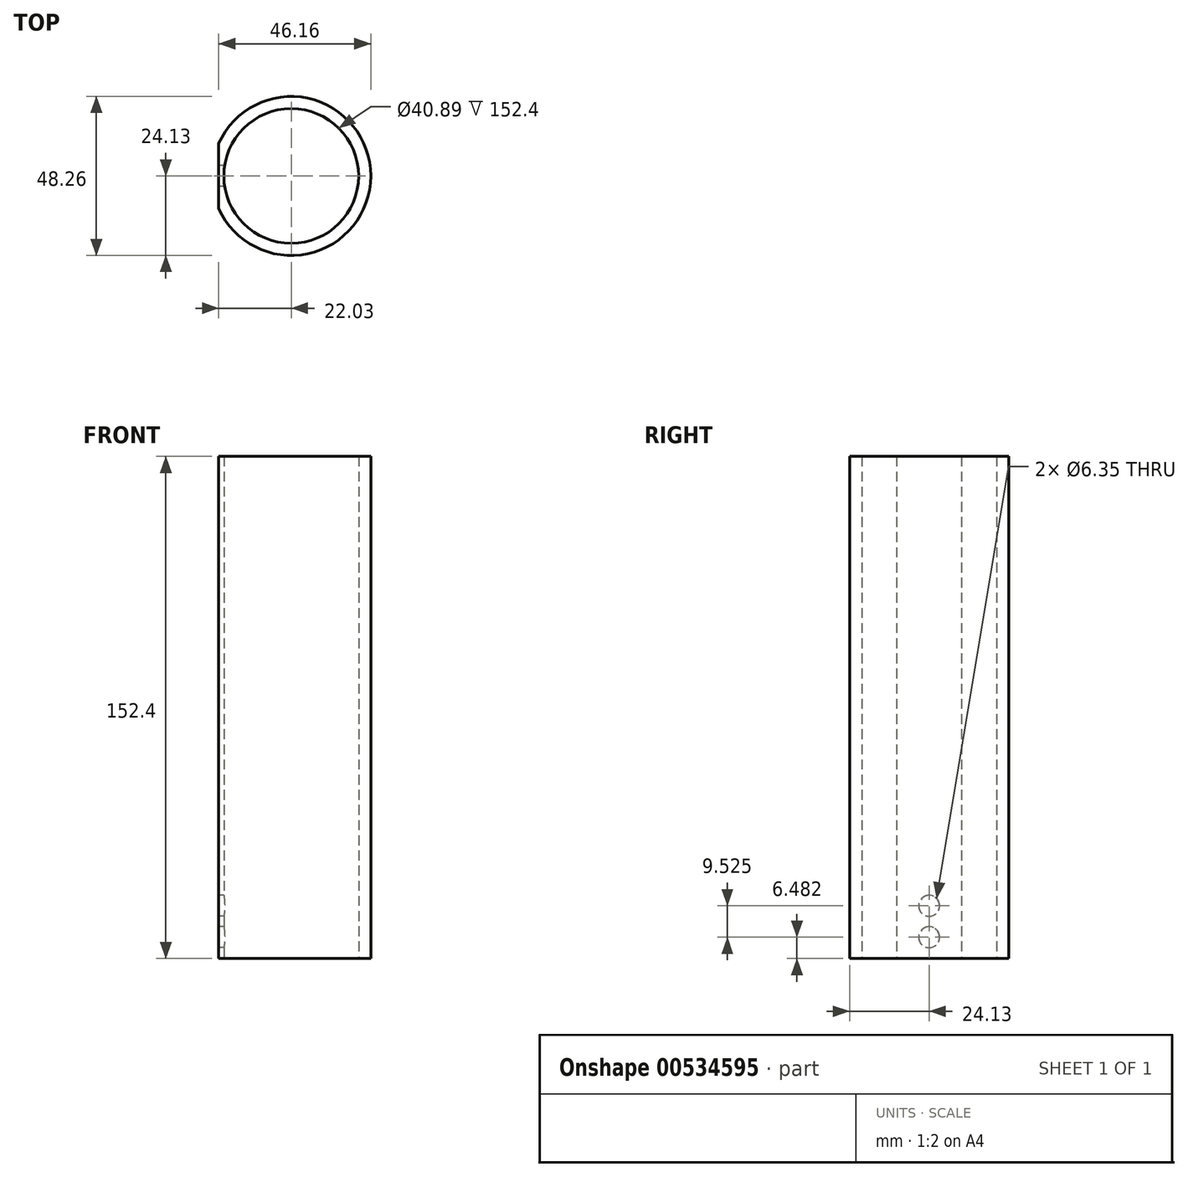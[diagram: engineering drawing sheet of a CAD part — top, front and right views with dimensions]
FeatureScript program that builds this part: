
annotation { "Feature Type Name" : "Feature", "Feature Type Description" : "" }
export const myFeature = defineFeature(function(context is Context, id is Id, definition is map)
    precondition{}
    {
        {
            var Q0;
            Q0=qCreatedBy(makeId("Top.planeOp"),FACE);
            var sketch = newSketch(context, id + "F0", { "sketchPlane" : qUnion([Q0])});
            skCircle(sketch, "E0", {"center": v(0, 0) * mm, "radius": 20.45 * mm});
            skCircle(sketch, "E1", {"center": v(0, 0) * mm, "radius": 24.13 * mm});
            skLineSegment(sketch, "E2.left", {"start": v(-22.03, 9.85) * mm, "end": v(-22.03, -9.85) * mm});
            skSolve(sketch);
        }
        {
            var Q0;
            Q0=makeQuery(id+"F0.imprint","IMPRINT",FACE,{"disambiguationData":[TD([[makeQuery(id+"F0.imprint","IMPRINT",EDGE,{"derivedFrom":sQuery(id+"F0.wireOp",EDGE,"E0")}),-1.0]])]});
            extrude(context, id + "F1", {"entities" : qUnion([Q0]), "depth" : 152.4 * mm, "offsetDistance" : 25.4 * mm});
        }
        {
            var Q0;
            Q0=makeQuery(id+"F1.opExtrude","SWEPT_FACE",FACE,{"disambiguationData":[OSD([sQuery(id+"F0.wireOp",EDGE,"E2.left")])]});
            var sketch = newSketch(context, id + "F2", { "sketchPlane" : qUnion([Q0])});
            skCircle(sketch, "E3", {"center": v(0, 6.48) * mm, "radius": 3.18 * mm});
            skLineSegment(sketch, "E4", {"start": v(0, 9.66) * mm, "end": v(0, 16) * mm});
            skCircle(sketch, "E5", {"center": v(0, 16) * mm, "radius": 3.18 * mm});
            skSolve(sketch);
        }
        {
            var Q0;
            Q0=makeQuery(id+"F2.imprint","IMPRINT",FACE,{"disambiguationData":[TD([[makeQuery(id+"F2.imprint","IMPRINT",EDGE,{"derivedFrom":sQuery(id+"F2.wireOp",EDGE,"E5")}),1.0]])]});
            var Q1;
            Q1=makeQuery(id+"F2.imprint","IMPRINT",FACE,{"disambiguationData":[TD([[makeQuery(id+"F2.imprint","IMPRINT",EDGE,{"derivedFrom":sQuery(id+"F2.wireOp",EDGE,"E3")}),1.0]])]});
            extrude(context, id + "F3", {"entities" : qUnion([Q0, Q1]), "operationType" : NewBodyOperationType.REMOVE, "oppositeDirection" : true, "depth" : 25.4 * mm, "offsetDistance" : 25.4 * mm});
        }
    });
